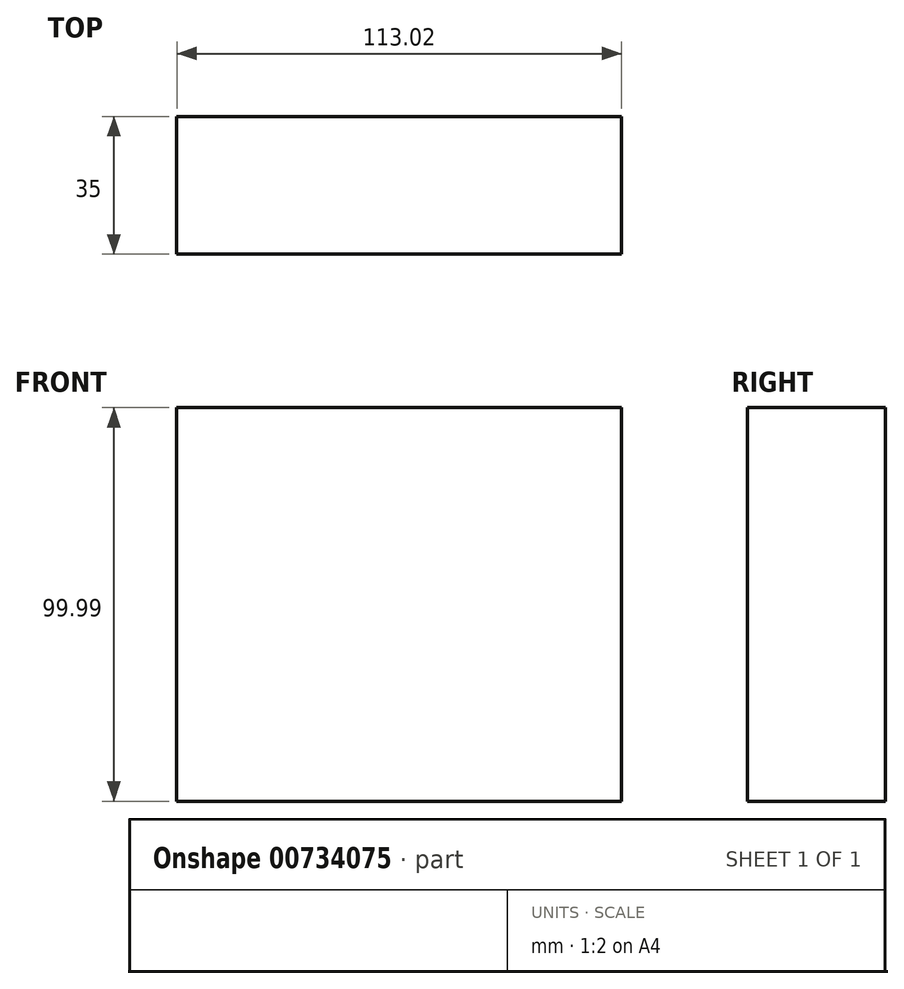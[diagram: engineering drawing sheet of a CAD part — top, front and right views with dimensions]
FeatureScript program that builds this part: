
annotation { "Feature Type Name" : "Feature", "Feature Type Description" : "" }
export const myFeature = defineFeature(function(context is Context, id is Id, definition is map)
    precondition{}
    {
        {
            var Q0;
            Q0=qCreatedBy(makeId("Front.planeOp"),FACE);
            var sketch = newSketch(context, id + "F0", { "sketchPlane" : qUnion([Q0])});
            skLineSegment(sketch, "E0.bottom", {"start": v(-65.3, 48.01) * mm, "end": v(47.73, 48.01) * mm});
            skLineSegment(sketch, "E0.top", {"start": v(-65.3, -51.98) * mm, "end": v(47.73, -51.98) * mm});
            skLineSegment(sketch, "E0.left", {"start": v(-65.3, 48.01) * mm, "end": v(-65.3, -51.98) * mm});
            skLineSegment(sketch, "E0.right", {"start": v(47.73, 48.01) * mm, "end": v(47.73, -51.98) * mm});
            skLineSegment(sketch, "E1.bottom", {"start": v(47.73, -51.98) * mm, "end": v(65.86, -51.98) * mm});
            skLineSegment(sketch, "E1.top", {"start": v(47.73, -55.38) * mm, "end": v(65.86, -55.38) * mm});
            skLineSegment(sketch, "E1.left", {"start": v(47.73, -51.98) * mm, "end": v(47.73, -55.38) * mm});
            skLineSegment(sketch, "E1.right", {"start": v(65.86, -51.98) * mm, "end": v(65.86, -55.38) * mm});
            skSolve(sketch);
        }
        {
            var Q0;
            Q0=makeQuery(id+"F0.imprint","IMPRINT",FACE,{"disambiguationData":[TD([[makeQuery(id+"F0.imprint","IMPRINT",EDGE,{"derivedFrom":sQuery(id+"F0.wireOp",EDGE,"E0.bottom")}),-1.0]])]});
            extrude(context, id + "F1", {"entities" : qUnion([Q0]), "depth" : 35 * mm, "offsetDistance" : 25 * mm});
        }
    });
